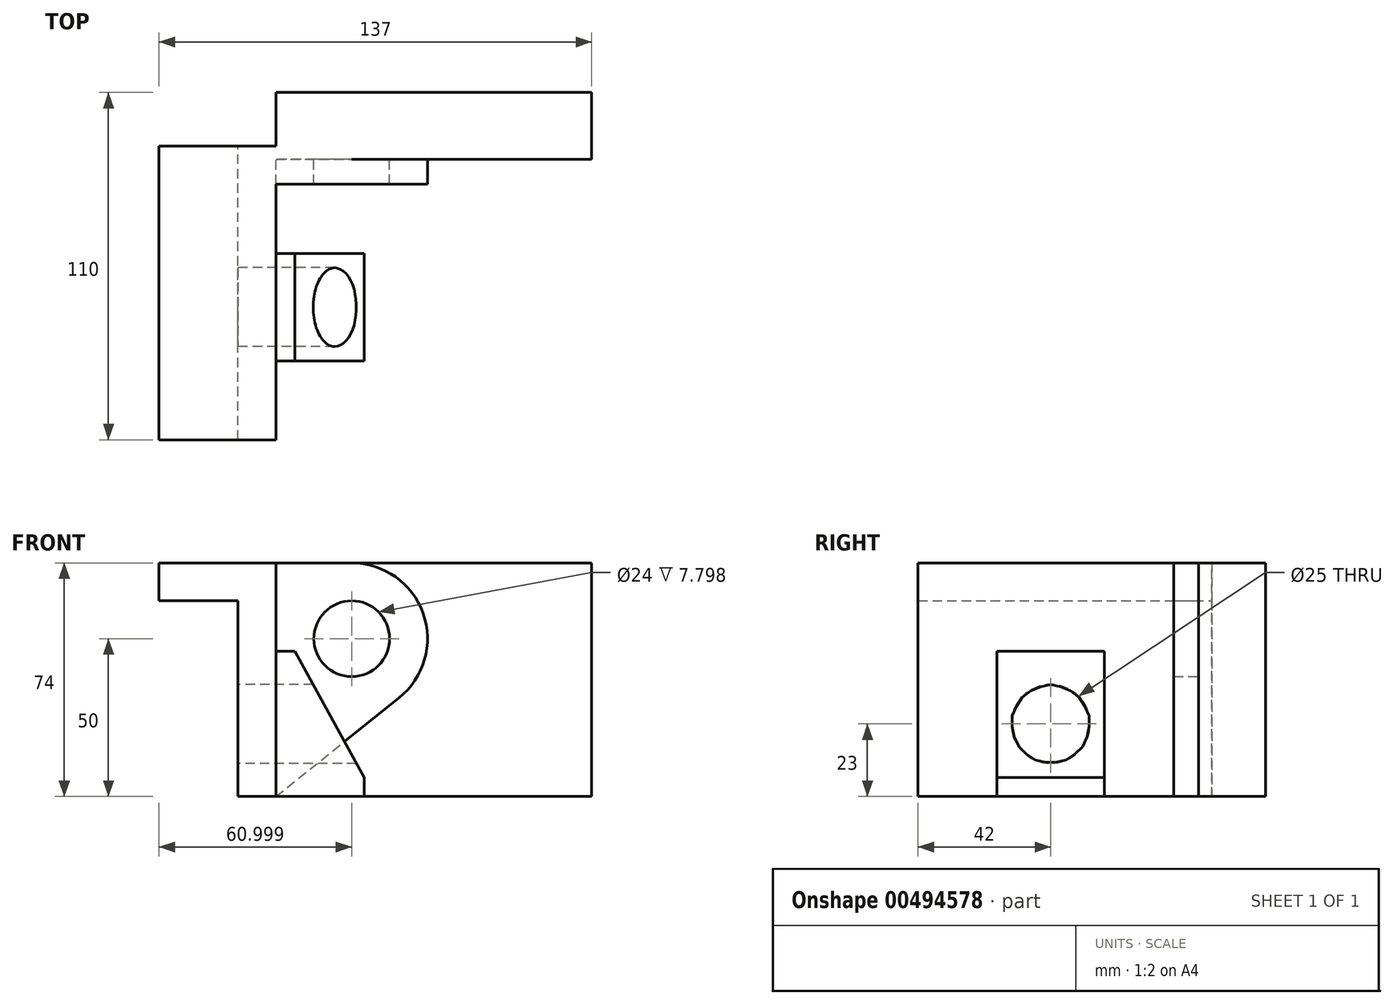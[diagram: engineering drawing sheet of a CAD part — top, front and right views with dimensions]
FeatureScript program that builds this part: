
annotation { "Feature Type Name" : "Feature", "Feature Type Description" : "" }
export const myFeature = defineFeature(function(context is Context, id is Id, definition is map)
    precondition{}
    {
        {
            var Q0;
            Q0=qCreatedBy(makeId("Front.planeOp"),FACE);
            var sketch = newSketch(context, id + "F0", { "sketchPlane" : qUnion([Q0])});
            skLineSegment(sketch, "E0", {"start": v(-40.9, 30.5) * mm, "end": v(-40.9, 18.5) * mm});
            skLineSegment(sketch, "E1", {"start": v(-40.9, 18.5) * mm, "end": v(-15.9, 18.5) * mm});
            skLineSegment(sketch, "E2", {"start": v(-15.9, 18.5) * mm, "end": v(-15.9, -43.5) * mm});
            skLineSegment(sketch, "E3", {"start": v(-15.9, -43.5) * mm, "end": v(-3.9, -43.5) * mm});
            skLineSegment(sketch, "E4", {"start": v(-3.9, -43.5) * mm, "end": v(-3.9, 30.5) * mm});
            skLineSegment(sketch, "E5", {"start": v(-3.9, 30.5) * mm, "end": v(-40.9, 30.5) * mm});
            skSolve(sketch);
        }
        {
            var Q0;
            Q0=makeQuery(id+"F0.imprint","IMPRINT",FACE,{"disambiguationData":[TD([[makeQuery(id+"F0.imprint","IMPRINT",EDGE,{"derivedFrom":sQuery(id+"F0.wireOp",EDGE,"E0")}),1.0]])]});
            extrude(context, id + "F1", {"entities" : qUnion([Q0]), "endBound" : BoundingType.SYMMETRIC, "depth" : 110 * mm, "offsetDistance" : 25 * mm});
        }
        {
            var Q0;
            Q0=makeQuery(id+"F1.opExtrude","SWEPT_FACE",FACE,{"disambiguationData":[OSD([sQuery(id+"F0.wireOp",EDGE,"E4")])]});
            var sketch = newSketch(context, id + "F2", { "sketchPlane" : qUnion([Q0])});
            skLineSegment(sketch, "E6.bottom", {"start": v(4, -43.5) * mm, "end": v(-30, -43.5) * mm});
            skLineSegment(sketch, "E6.top", {"start": v(4, 2.5) * mm, "end": v(-30, 2.5) * mm});
            skLineSegment(sketch, "E6.left", {"start": v(4, -43.5) * mm, "end": v(4, 2.5) * mm});
            skLineSegment(sketch, "E6.right", {"start": v(-30, -43.5) * mm, "end": v(-30, 2.5) * mm});
            skPoint(sketch, "E6.middle", {"position": v(-13, -20.5) * mm});
            skSolve(sketch);
        }
        {
            var Q0;
            Q0=makeQuery(id+"F2.imprint","IMPRINT",FACE,{"disambiguationData":[TD([[makeQuery(id+"F2.imprint","IMPRINT",EDGE,{"derivedFrom":sQuery(id+"F2.wireOp",EDGE,"E6.bottom")}),1.0]])]});
            extrude(context, id + "F3", {"entities" : qUnion([Q0]), "operationType" : NewBodyOperationType.ADD, "depth" : 28 * mm, "offsetDistance" : 25 * mm});
        }
        {
            var Q0;
            Q0=makeQuery(id+"F3.opExtrude","SWEPT_FACE",FACE,{"disambiguationData":[OSD([sQuery(id+"F2.wireOp",EDGE,"E6.right")])]});
            var sketch = newSketch(context, id + "F4", { "sketchPlane" : qUnion([Q0])});
            skLineSegment(sketch, "E7", {"start": v(-3.9, 2.5) * mm, "end": v(2.1, 2.5) * mm});
            skLineSegment(sketch, "E8", {"start": v(24.1, -43.5) * mm, "end": v(24.1, -37.5) * mm});
            skLineSegment(sketch, "E9", {"start": v(2.1, 2.5) * mm, "end": v(24.1, -37.5) * mm});
            skSolve(sketch);
        }
        {
            var Q0;
            {var subQ0=sQuery(id+"F4.wireOp",EDGE,"E9");Q0=makeQuery(id+"F4.imprint","IMPRINT",FACE,{"disambiguationData":[TD([[makeQuery(id+"F4.imprint","IMPRINT",EDGE,{"derivedFrom":subQ0}),1.0]])]});}
            extrude(context, id + "F5", {"entities" : qUnion([Q0]), "operationType" : NewBodyOperationType.REMOVE, "oppositeDirection" : true, "depth" : 34 * mm, "offsetDistance" : 25 * mm});
        }
        {
            var Q0;
            Q0=makeQuery(id+"F1.opExtrude","SWEPT_FACE",FACE,{"disambiguationData":[OSD([sQuery(id+"F0.wireOp",EDGE,"E2")])]});
            var sketch = newSketch(context, id + "F6", { "sketchPlane" : qUnion([Q0])});
            skCircle(sketch, "E10", {"center": v(13, -20.5) * mm, "radius": 12.5 * mm});
            skLineSegment(sketch, "E11", {"start": v(-55, -43.5) * mm, "end": v(-24, -43.5) * mm});
            skLineSegment(sketch, "E12", {"start": v(-24, -43.5) * mm, "end": v(0.83, -43.5) * mm});
            skLineSegment(sketch, "E13", {"start": v(0.83, -43.5) * mm, "end": v(-24, -43.5) * mm});
            skSolve(sketch);
        }
        {
            var Q0;
            Q0=makeQuery(id+"F1.opExtrude","SWEPT_FACE",FACE,{"disambiguationData":[OSD([sQuery(id+"F0.wireOp",EDGE,"E4")])]});
            var sketch = newSketch(context, id + "F7", { "sketchPlane" : qUnion([Q0])});
            skSolve(sketch);
        }
        {
            var Q0;
            Q0=makeQuery(id+"F6.imprint","IMPRINT",FACE,{"disambiguationData":[TD([[makeQuery(id+"F6.imprint","IMPRINT",EDGE,{"derivedFrom":sQuery(id+"F6.wireOp",EDGE,"E10")}),1.0]])]});
            extrude(context, id + "F8", {"entities" : qUnion([Q0]), "operationType" : NewBodyOperationType.REMOVE, "oppositeDirection" : true, "depth" : 100 * mm, "offsetDistance" : 25 * mm});
        }
        {
            var Q0;
            {var subQ0=sQuery(id+"F0.wireOp",EDGE,"E4");Q0=makeQuery(id+"F7.imprint","IMPRINT",FACE,{"disambiguationData":[TD([[makeQuery(id+"F7.imprint","IMPRINT",EDGE,{"derivedFrom":makeQuery(id+"F1.opExtrude","CAP_EDGE",EDGE,{"disambiguationData":[OSD([subQ0])],"isStart":true})}),1.0]])]});}
            var sketch = newSketch(context, id + "F9", { "sketchPlane" : qUnion([Q0])});
            skLineSegment(sketch, "E14.0", {"start": v(-55, 30.5) * mm, "end": v(55, 30.5) * mm});
            skLineSegment(sketch, "E15.0", {"start": v(55, -43.5) * mm, "end": v(55, 30.5) * mm});
            skLineSegment(sketch, "E16.0", {"start": v(4, -43.5) * mm, "end": v(55, -43.5) * mm});
            skLineSegment(sketch, "E17", {"start": v(33.8, -43.5) * mm, "end": v(33.8, 30.5) * mm});
            skSolve(sketch);
        }
        {
            var Q0;
            Q0=makeQuery(id+"F1.opExtrude","CAP_FACE",FACE,{"disambiguationData":[OSD([sQuery(id+"F0.wireOp",EDGE,"E0"),sQuery(id+"F0.wireOp",EDGE,"E1"),sQuery(id+"F0.wireOp",EDGE,"E2"),sQuery(id+"F0.wireOp",EDGE,"E3"),sQuery(id+"F0.wireOp",EDGE,"E4"),sQuery(id+"F0.wireOp",EDGE,"E5")])],"isStart":true});
            extrude(context, id + "F10", {"entities" : qUnion([Q0]), "operationType" : NewBodyOperationType.REMOVE, "oppositeDirection" : true, "depth" : 17 * mm, "offsetDistance" : 25 * mm});
        }
        {
            var Q0;
            Q0=makeQuery(id+"F1.opExtrude","SWEPT_FACE",FACE,{"disambiguationData":[OSD([sQuery(id+"F0.wireOp",EDGE,"E4")])]});
            var sketch = newSketch(context, id + "F11", { "sketchPlane" : qUnion([Q0])});
            skLineSegment(sketch, "E18.bottom", {"start": v(38, 30.5) * mm, "end": v(26, 30.5) * mm});
            skLineSegment(sketch, "E18.top", {"start": v(38, -43.5) * mm, "end": v(26, -43.5) * mm});
            skLineSegment(sketch, "E18.left", {"start": v(38, 30.5) * mm, "end": v(38, -43.5) * mm});
            skLineSegment(sketch, "E18.right", {"start": v(26, 30.5) * mm, "end": v(26, -43.5) * mm});
            skSolve(sketch);
        }
        {
            var Q0;
            Q0=makeQuery(id+"F11.imprint","IMPRINT",FACE,{"disambiguationData":[TD([[makeQuery(id+"F11.imprint","IMPRINT",EDGE,{"derivedFrom":sQuery(id+"F11.wireOp",EDGE,"E18.bottom")}),-1.0]])]});
            extrude(context, id + "F12", {"entities" : qUnion([Q0]), "operationType" : NewBodyOperationType.ADD, "depth" : (25 - 1) * mm, "offsetDistance" : 25 * mm});
        }
        {
            var Q0;
            Q0=makeQuery(id+"F12.boolean.opBoolean","MERGE",FACE,{"derivedFrom":[makeQuery(id+"F10.boolean.opBoolean","COPY",FACE,{"derivedFrom":makeQuery(id+"F10.opExtrude","CAP_FACE",FACE,{"disambiguationData":[OSD([sQuery(id+"F0.wireOp",EDGE,"E0"),sQuery(id+"F0.wireOp",EDGE,"E1"),sQuery(id+"F0.wireOp",EDGE,"E2"),sQuery(id+"F0.wireOp",EDGE,"E3"),sQuery(id+"F0.wireOp",EDGE,"E4"),sQuery(id+"F0.wireOp",EDGE,"E5")])],"isStart":false})}),makeQuery(id+"F12.opExtrude","SWEPT_FACE",FACE,{"disambiguationData":[OSD([sQuery(id+"F11.wireOp",EDGE,"E18.left")])]})]});
            var sketch = newSketch(context, id + "F13", { "sketchPlane" : qUnion([Q0])});
            skLineSegment(sketch, "E19", {"start": v(-20.1, 30.5) * mm, "end": v(-20.1, 6.5) * mm});
            skCircle(sketch, "E20", {"center": v(-20.1, 6.5) * mm, "radius": 24 * mm});
            skLineSegment(sketch, "E21", {"start": v(15.9, -43.5) * mm, "end": v(3.9, -43.5) * mm});
            skLineSegment(sketch, "E22", {"start": v(3.9, -43.5) * mm, "end": v(-35.11, -12.24) * mm});
            skSolve(sketch);
        }
        {
            var Q0;
            {var subQ0=sQuery(id+"F13.wireOp",EDGE,"E22");var subQ1=sQuery(id+"F11.wireOp",EDGE,"E18.left");var subQ4=makeQuery(id+"F12.opExtrude","CAP_EDGE",EDGE,{"disambiguationData":[OSD([subQ1])],"isStart":false});var subQ5=makeQuery(id+"F13.imprint","INTERSECT",VERTEX,{"derivedFrom":[subQ4,subQ0]});Q0=makeQuery(id+"F13.imprint","IMPRINT",FACE,{"disambiguationData":[TD([[makeQuery(id+"F13.imprint","IMPRINT",EDGE,{"disambiguationData":[TD([[subQ5,1.0]])],"derivedFrom":subQ4}),-1.0]])]});}
            extrude(context, id + "F14", {"entities" : qUnion([Q0]), "operationType" : NewBodyOperationType.REMOVE, "oppositeDirection" : true, "depth" : 12 * mm, "offsetDistance" : 25 * mm});
        }
        {
            var Q0;
            Q0 = qSketchRegion(id + "F13", true);
            var Q1;
            {var subQ0=sQuery(id+"F13.wireOp",EDGE,"E22");var subQ1=sQuery(id+"F13.wireOp",EDGE,"E20");var subQ2=makeQuery(id+"F13.imprint","INTERSECT",VERTEX,{"derivedFrom":[subQ1,subQ0]});Q1=makeQuery(id+"F13.imprint","IMPRINT",FACE,{"disambiguationData":[TD([[makeQuery(id+"F13.imprint","IMPRINT",EDGE,{"disambiguationData":[TD([[subQ2,-1.0]])],"derivedFrom":subQ1}),-1.0]])]});}
            extrude(context, id + "F15", {"entities" : qUnion([Q0, Q1]), "operationType" : NewBodyOperationType.ADD, "oppositeDirection" : true, "depth" : 12 * mm, "offsetDistance" : 25 * mm});
        }
        {
            var Q0;
            {var subQ0=sQuery(id+"F11.wireOp",EDGE,"E18.left");Q0=makeQuery(id+"F15.boolean.opBoolean","MERGE",FACE,{"derivedFrom":[makeQuery(id+"F12.boolean.opBoolean","MERGE",FACE,{"derivedFrom":[makeQuery(id+"F10.boolean.opBoolean","COPY",FACE,{"derivedFrom":makeQuery(id+"F10.opExtrude","CAP_FACE",FACE,{"disambiguationData":[OSD([sQuery(id+"F0.wireOp",EDGE,"E0"),sQuery(id+"F0.wireOp",EDGE,"E1"),sQuery(id+"F0.wireOp",EDGE,"E2"),sQuery(id+"F0.wireOp",EDGE,"E3"),sQuery(id+"F0.wireOp",EDGE,"E4"),sQuery(id+"F0.wireOp",EDGE,"E5")])],"isStart":false})}),makeQuery(id+"F12.opExtrude","SWEPT_FACE",FACE,{"disambiguationData":[OSD([subQ0])]})]}),makeQuery(id+"F15.opExtrude","CAP_FACE",FACE,{"disambiguationData":[OSD([subQ0,sQuery(id+"F13.wireOp",EDGE,"E20"),sQuery(id+"F13.wireOp",EDGE,"E22")])],"isStart":true})]});}
            var sketch = newSketch(context, id + "F16", { "sketchPlane" : qUnion([Q0])});
            skCircle(sketch, "E23", {"center": v(-20.1, 6.5) * mm, "radius": 12 * mm});
            skSolve(sketch);
        }
        {
            var Q0;
            Q0=makeQuery(id+"F16.imprint","IMPRINT",FACE,{"disambiguationData":[TD([[makeQuery(id+"F16.imprint","IMPRINT",EDGE,{"derivedFrom":sQuery(id+"F16.wireOp",EDGE,"E23")}),1.0]])]});
            extrude(context, id + "F17", {"entities" : qUnion([Q0]), "operationType" : NewBodyOperationType.REMOVE, "oppositeDirection" : true, "depth" : 25 * mm, "offsetDistance" : 25 * mm});
        }
        {
            var Q0;
            Q0 = qSketchRegion(id + "F9", true);
            extrude(context, id + "F18", {"entities" : qUnion([Q0]), "operationType" : NewBodyOperationType.ADD, "depth" : 100 * mm, "offsetDistance" : 25 * mm});
        }
    });
